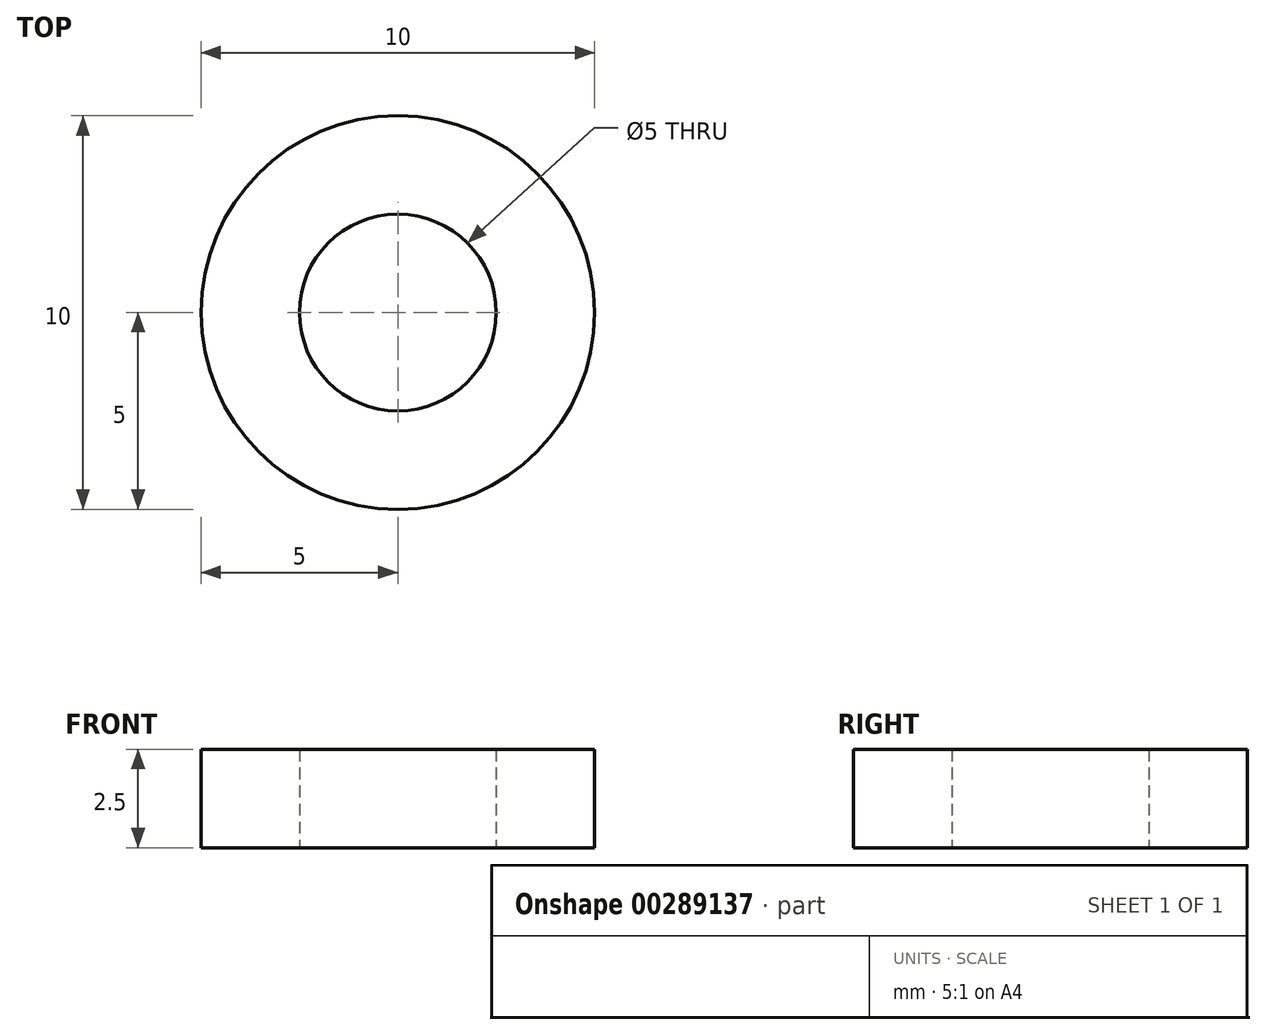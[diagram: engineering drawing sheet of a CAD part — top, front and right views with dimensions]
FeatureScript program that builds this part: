
annotation { "Feature Type Name" : "Feature", "Feature Type Description" : "" }
export const myFeature = defineFeature(function(context is Context, id is Id, definition is map)
    precondition{}
    {
        {
            var Q0;
            Q0=qCreatedBy(makeId("Top.planeOp"),FACE);
            var sketch = newSketch(context, id + "F0", { "sketchPlane" : qUnion([Q0])});
            skCircle(sketch, "E0", {"center": v(0, 0) * mm, "radius": 5 * mm});
            skCircle(sketch, "E1", {"center": v(0, 0) * mm, "radius": 2.5 * mm});
            skSolve(sketch);
        }
        {
            var Q0;
            Q0 = qSketchRegion(id + "F0", true);
            extrude(context, id + "F1", {"entities" : qUnion([Q0]), "depth" : 2.5 * mm});
        }
    });
